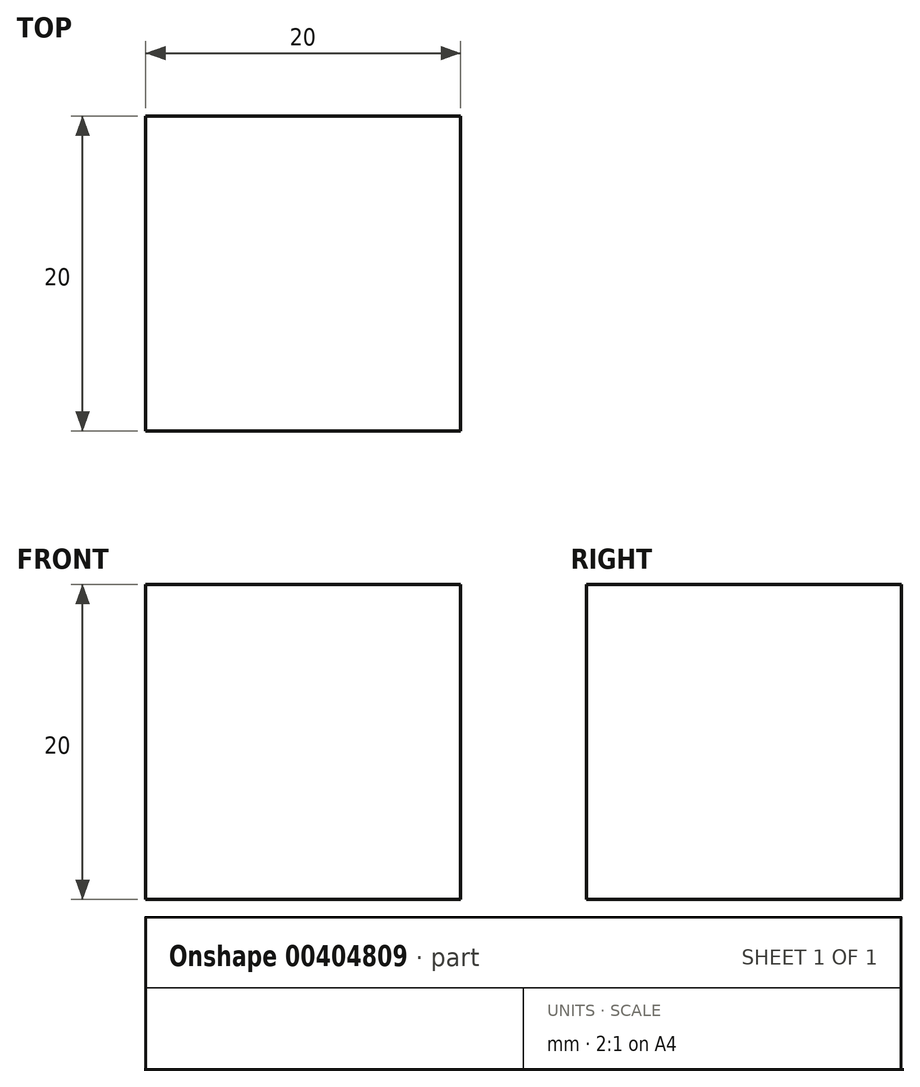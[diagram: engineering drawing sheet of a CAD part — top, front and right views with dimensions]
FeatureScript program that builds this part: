
annotation { "Feature Type Name" : "Feature", "Feature Type Description" : "" }
export const myFeature = defineFeature(function(context is Context, id is Id, definition is map)
    precondition{}
    {
        {
            var Q0;
            Q0=qCreatedBy(makeId("Top.planeOp"),FACE);
            var sketch = newSketch(context, id + "F0", { "sketchPlane" : qUnion([Q0])});
            skLineSegment(sketch, "E0.bottom", {"start": v(-10, 10) * mm, "end": v(10, 10) * mm});
            skLineSegment(sketch, "E0.top", {"start": v(-10, -10) * mm, "end": v(10, -10) * mm});
            skLineSegment(sketch, "E0.left", {"start": v(-10, 10) * mm, "end": v(-10, -10) * mm});
            skLineSegment(sketch, "E0.right", {"start": v(10, 10) * mm, "end": v(10, -10) * mm});
            skSolve(sketch);
        }
        {
            var Q0;
            Q0 = qSketchRegion(id + "F0", true);
            extrude(context, id + "F1", {"entities" : qUnion([Q0]), "depth" : 20 * mm});
        }
    });
